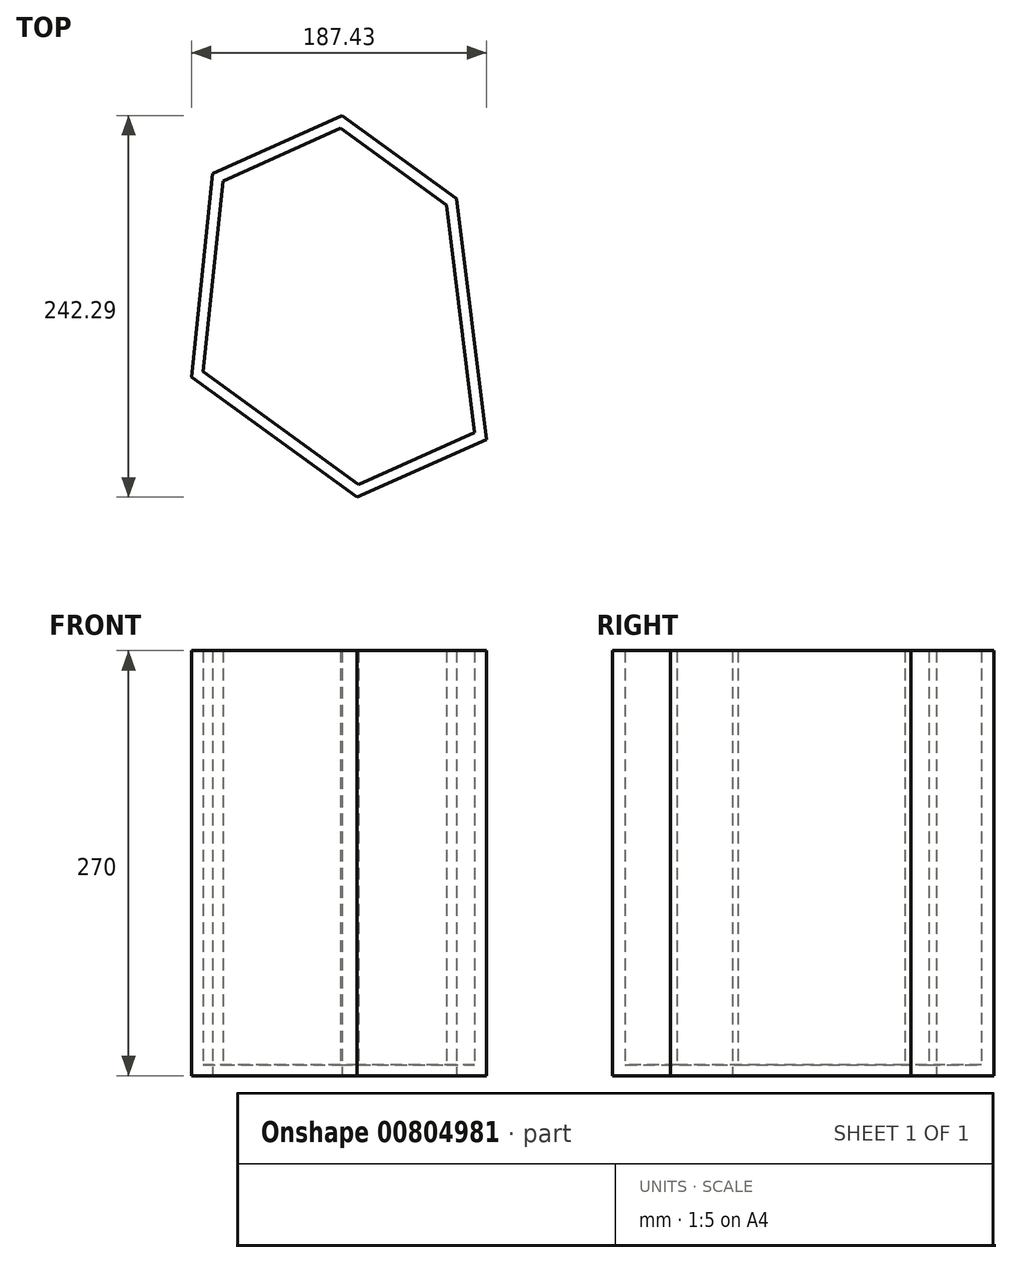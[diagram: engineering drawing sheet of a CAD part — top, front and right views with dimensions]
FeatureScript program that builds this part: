
annotation { "Feature Type Name" : "Feature", "Feature Type Description" : "" }
export const myFeature = defineFeature(function(context is Context, id is Id, definition is map)
    precondition{}
    {
        {
            var Q0;
            Q0=qCreatedBy(makeId("Top.planeOp"),FACE);
            var sketch = newSketch(context, id + "F0", { "sketchPlane" : qUnion([Q0])});
            skLineSegment(sketch, "E0.0", {"start": v(105.25, -76.3) * mm, "end": v(23.07, -113) * mm});
            skLineSegment(sketch, "E0.1", {"start": v(23.07, -113) * mm, "end": v(-82.18, -36.7) * mm});
            skLineSegment(sketch, "E0.2", {"start": v(-82.18, -36.7) * mm, "end": v(-68.73, 92.61) * mm});
            skLineSegment(sketch, "E0.3", {"start": v(-68.73, 92.61) * mm, "end": v(13.46, 129.3) * mm});
            skLineSegment(sketch, "E0.4", {"start": v(13.46, 129.3) * mm, "end": v(86.32, 76.48) * mm});
            skLineSegment(sketch, "E0.5", {"start": v(86.32, 76.48) * mm, "end": v(105.25, -76.3) * mm});
            skPoint(sketch, "E0.0.midPoint", {"position": v(64.16, -94.65) * mm});
            skSolve(sketch);
        }
        {
            var Q0;
            Q0 = qSketchRegion(id + "F0", true);
            extrude(context, id + "F1", {"entities" : qUnion([Q0]), "depth" : 270 * mm, "offsetDistance" : 25 * mm});
        }
        {
            var Q0;
            Q0=makeQuery(id+"F1.opExtrude","CAP_FACE",FACE,{"disambiguationData":[OSD([sQuery(id+"F0.wireOp",EDGE,"E0.0"),sQuery(id+"F0.wireOp",EDGE,"E0.1"),sQuery(id+"F0.wireOp",EDGE,"E0.2"),sQuery(id+"F0.wireOp",EDGE,"E0.3"),sQuery(id+"F0.wireOp",EDGE,"E0.4"),sQuery(id+"F0.wireOp",EDGE,"E0.5")])],"isStart":false});
            shell(context, id + "F2", {"entities" : qUnion([Q0]), "thickness" : 7 * mm});
        }
    });
